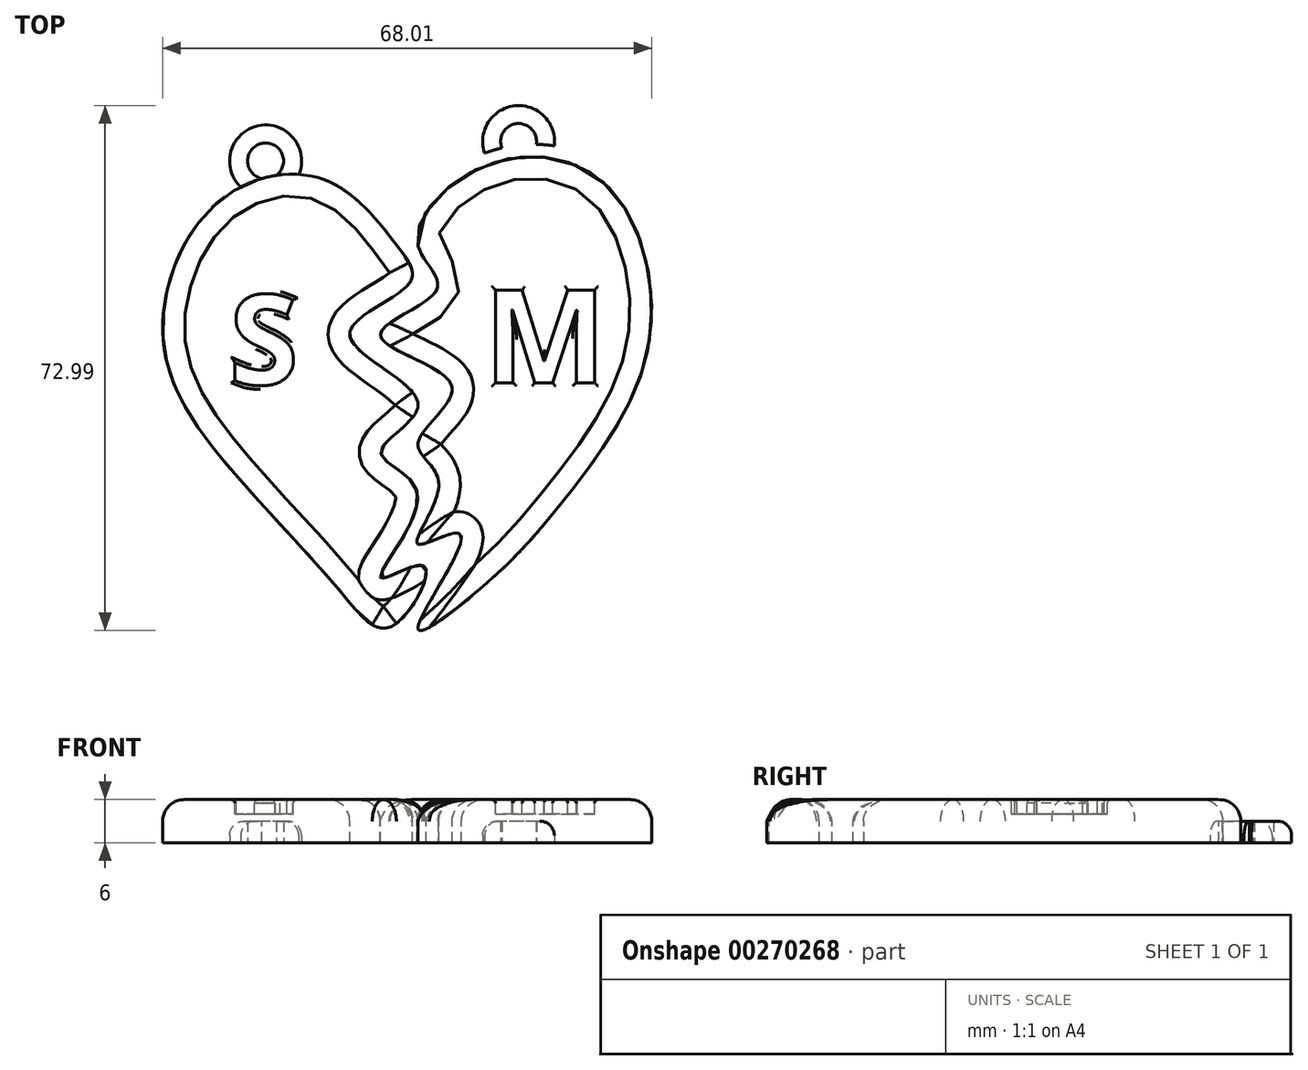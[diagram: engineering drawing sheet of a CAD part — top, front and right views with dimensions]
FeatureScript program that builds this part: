
annotation { "Feature Type Name" : "Feature", "Feature Type Description" : "" }
export const myFeature = defineFeature(function(context is Context, id is Id, definition is map)
    precondition{}
    {
        {
            var Q0;
            Q0=qCreatedBy(makeId("Top.planeOp"),FACE);
            var sketch = newSketch(context, id + "F0", { "sketchPlane" : qUnion([Q0])});
            skFitSpline(sketch, "E0", {"points": [v(0, 15.4) * mm, v(5.56, 24.51) * mm, v(18.32, 27.63) * mm, v(28.55, 21) * mm, v(32.37, 3.71) * mm, v(26.9, -10.83) * mm, v(18.6, -22.02) * mm, v(9.67, -31.42) * mm, v(0, -37.73) * mm, v(5.91, -24.74) * mm, v(0, -26.09) * mm, v(2.89, -17.67) * mm, v(0, -12.03) * mm, v(4.66, -4.04) * mm, v(-5.2, 2.94) * mm, v(2.58, 9.22) * mm, v(0, 15.4) * mm]});
            skFitSpline(sketch, "E1", {"points": [v(-2.93, 15.4) * mm, v(-12.96, 24.54) * mm, v(-27.93, 21.38) * mm, v(-35.49, 2.94) * mm, v(-27.3, -14.15) * mm, v(-11.03, -32.4) * mm, v(-3.48, -37.42) * mm, v(0.77, -29.13) * mm, v(-5.2, -30.8) * mm, v(-0.07, -19.15) * mm, v(-5.2, -13.28) * mm, v(0, -6.6) * mm, v(-9.5, 2.94) * mm, v(-1.28, 10.1) * mm, v(-2.93, 15.4) * mm]});
            skSolve(sketch);
        }
        {
            var Q0;
            Q0=makeQuery(id+"F0.imprint","IMPRINT",FACE,{"disambiguationData":[TD([[makeQuery(id+"F0.imprint","IMPRINT",EDGE,{"derivedFrom":sQuery(id+"F0.wireOp",EDGE,"E1")}),1.0]])]});
            var Q1;
            Q1=makeQuery(id+"F0.imprint","IMPRINT",FACE,{"disambiguationData":[TD([[makeQuery(id+"F0.imprint","IMPRINT",EDGE,{"derivedFrom":sQuery(id+"F0.wireOp",EDGE,"E0")}),-1.0]])]});
            extrude(context, id + "F1", {"entities" : qUnion([Q0, Q1]), "depth" : 6 * mm});
        }
        {
            var Q0;
            Q0=makeQuery(id+"F1.opExtrude","CAP_EDGE",EDGE,{"disambiguationData":[OSD([sQuery(id+"F0.wireOp",EDGE,"E1")])],"isStart":false});
            fillet(context, id + "F2", {"entities" : qUnion([Q0]), "radius" : 3 * mm, "tangentPropagation" : true, "allowEdgeOverflow" : false});
        }
        {
            var Q0;
            Q0=makeQuery(id+"F1.opExtrude","CAP_EDGE",EDGE,{"disambiguationData":[OSD([sQuery(id+"F0.wireOp",EDGE,"E0")])],"isStart":false});
            fillet(context, id + "F3", {"entities" : qUnion([Q0]), "radius" : 3 * mm, "tangentPropagation" : true, "allowEdgeOverflow" : false});
        }
        {
            var Q0;
            Q0=makeQuery(id+"F2.opFillet","SPLIT",FACE,{"disambiguationData":[OD(0.0)],"derivedFrom":makeQuery(id+"F1.opExtrude","CAP_FACE",FACE,{"disambiguationData":[OSD([sQuery(id+"F0.wireOp",EDGE,"E1")])],"isStart":false})});
            var sketch = newSketch(context, id + "F4", { "sketchPlane" : qUnion([Q0])});
            skText(sketch, "E2", { "text": "S", "fontName": "OpenSans-Bold.ttf"});
            skText(sketch, "E3", { "text": "M", "fontName": "OpenSans-Bold.ttf"});
            const initialGuessF4  = {"E2": [-0.02626, -0.00391, 1, 0, 0.01258], "E3": [0.00915, -0.00364, 1, 0, 0.01299]};
            skSetInitialGuess(sketch, initialGuessF4);
            skSolve(sketch);
        }
        {
            var Q0;
            Q0=makeQuery(id+"F4.imprint","IMPRINT",FACE,{"disambiguationData":[TD([[makeQuery(id+"F4.imprint","IMPRINT",EDGE,{"derivedFrom":sQuery(id+"F4.wireOp",EDGE,"E2.sketch_text.stroke-0")}),-1.0]])]});
            extrude(context, id + "F5", {"entities" : qUnion([Q0]), "operationType" : NewBodyOperationType.REMOVE, "oppositeDirection" : true, "depth" : 2 * mm});
        }
        {
            var Q0;
            Q0=makeQuery(id+"F4.imprint","IMPRINT",FACE,{"disambiguationData":[TD([[makeQuery(id+"F4.imprint","IMPRINT",EDGE,{"derivedFrom":sQuery(id+"F4.wireOp",EDGE,"E3.sketch_text.stroke-0")}),-1.0]])]});
            extrude(context, id + "F6", {"entities" : qUnion([Q0]), "operationType" : NewBodyOperationType.REMOVE, "oppositeDirection" : true, "depth" : 2 * mm});
        }
        {
            var Q0;
            Q0=makeQuery(id+"F0.imprint","IMPRINT",FACE,{"disambiguationData":[TD([[makeQuery(id+"F0.imprint","IMPRINT",EDGE,{"derivedFrom":sQuery(id+"F0.wireOp",EDGE,"E1")}),1.0]])]});
            var sketch = newSketch(context, id + "F7", { "sketchPlane" : qUnion([Q0])});
            skFitSpline(sketch, "E4.0.0", {"points": [v(-2.93, 15.4) * mm, v(-5.4, 18.63) * mm, v(-11.98, 27.4) * mm, v(-30.38, 23.8) * mm, v(-38.64, 2) * mm, v(-27.94, -14.66) * mm, v(-11.7, -30.8) * mm, v(-3.9, -41.91) * mm, v(4.72, -25.06) * mm, v(-10.62, -35.18) * mm, v(5.59, -17.5) * mm, v(-10.24, -13.82) * mm, v(6.89, -6.12) * mm, v(-17.27, 3.08) * mm, v(1.79, 9.43) * mm, v(-1.33, 13.35) * mm, v(-2.93, 15.4) * mm]});
            skFitSpline(sketch, "E5.0.0", {"points": [v(0, 15.4) * mm, v(0.62, 13.02) * mm, v(7.05, 8.67) * mm, v(-12.93, 2.59) * mm, v(11.37, -2.88) * mm, v(-3.95, -12.43) * mm, v(6.4, -16.56) * mm, v(-4.35, -29.67) * mm, v(11.73, -19.8) * mm, v(-6.37, -44.51) * mm, v(11.79, -30.11) * mm, v(18.31, -22.5) * mm, v(27.54, -10.9) * mm, v(34.21, 3.2) * mm, v(30.44, 22.1) * mm, v(18.6, 29.33) * mm, v(5.23, 26.2) * mm, v(-0.78, 18.42) * mm, v(0, 15.4) * mm]});
            skArc(sketch, "E6", {"start": v(-16.57, 25.31) * mm, "mid": v(-22.25, 32.07) * mm, "end": v(-24.66, 23.57) * mm});
            skCircle(sketch, "E7", {"center": v(-21.2, 27.18) * mm, "radius": 2.5 * mm});
            skArc(sketch, "E8", {"start": v(18.45, 27.61) * mm, "mid": v(13.5, 34.86) * mm, "end": v(10.06, 26.8) * mm});
            skCircle(sketch, "E9", {"center": v(14, 29.88) * mm, "radius": 2.5 * mm});
            skSolve(sketch);
        }
        {
            var Q0;
            {var subQ0=sQuery(id+"F7.wireOp",EDGE,"E6");Q0=makeQuery(id+"F7.imprint","IMPRINT",FACE,{"disambiguationData":[TD([[makeQuery(id+"F7.imprint","IMPRINT",EDGE,{"derivedFrom":subQ0}),1.0]])]});}
            var Q1;
            {var subQ0=sQuery(id+"F7.wireOp",EDGE,"E8");Q1=makeQuery(id+"F7.imprint","IMPRINT",FACE,{"disambiguationData":[TD([[makeQuery(id+"F7.imprint","IMPRINT",EDGE,{"derivedFrom":subQ0}),1.0]])]});}
            extrude(context, id + "F8", {"entities" : qUnion([Q0, Q1]), "operationType" : NewBodyOperationType.ADD, "depth" : 3 * mm});
        }
        {
            var Q0;
            Q0=makeQuery(id+"F8.opExtrude","CAP_EDGE",EDGE,{"disambiguationData":[OSD([sQuery(id+"F7.wireOp",EDGE,"E6")])],"isStart":false});
            var Q1;
            Q1=makeQuery(id+"F8.opExtrude","CAP_EDGE",EDGE,{"disambiguationData":[OSD([sQuery(id+"F7.wireOp",EDGE,"E8")])],"isStart":false});
            fillet(context, id + "F9", {"entities" : qUnion([Q0, Q1]), "radius" : 2 * mm, "tangentPropagation" : true, "allowEdgeOverflow" : false});
        }
        {
            var Q0;
            Q0=makeQuery(id+"F2.opFillet","SPLIT",FACE,{"disambiguationData":[OD(0.0)],"derivedFrom":makeQuery(id+"F1.opExtrude","CAP_FACE",FACE,{"disambiguationData":[OSD([sQuery(id+"F0.wireOp",EDGE,"E1")])],"isStart":false})});
            fillet(context, id + "F10", {"entities" : qUnion([Q0]), "radius" : 0.5 * mm, "tangentPropagation" : true, "allowEdgeOverflow" : false});
        }
        {
            var Q0;
            Q0=makeQuery(id+"F1.opExtrude","CAP_FACE",FACE,{"disambiguationData":[OSD([sQuery(id+"F0.wireOp",EDGE,"E0")])],"isStart":false});
            fillet(context, id + "F11", {"entities" : qUnion([Q0]), "radius" : 0.5 * mm, "tangentPropagation" : true, "allowEdgeOverflow" : false});
        }
    });
